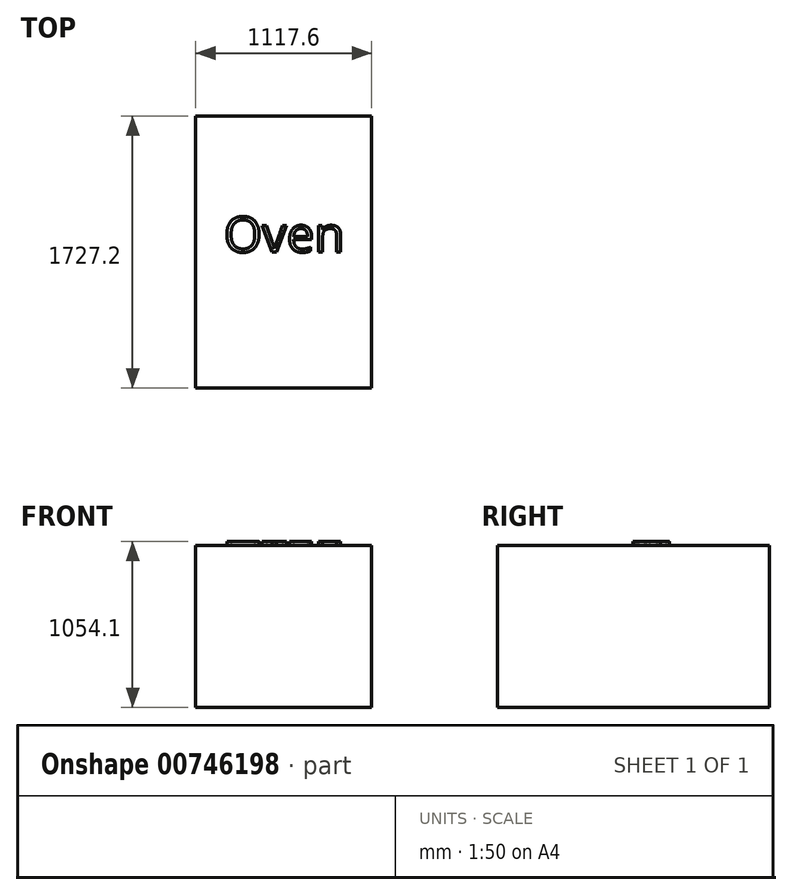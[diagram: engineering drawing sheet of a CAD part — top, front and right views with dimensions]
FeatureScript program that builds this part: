
annotation { "Feature Type Name" : "Feature", "Feature Type Description" : "" }
export const myFeature = defineFeature(function(context is Context, id is Id, definition is map)
    precondition{}
    {
        {
            var Q0;
            Q0=qCreatedBy(makeId("Top.planeOp"),FACE);
            var sketch = newSketch(context, id + "F0", { "sketchPlane" : qUnion([Q0])});
            skLineSegment(sketch, "E0.bottom", {"start": v(558.8, -863.6) * mm, "end": v(-558.8, -863.6) * mm});
            skLineSegment(sketch, "E0.top", {"start": v(558.8, 863.6) * mm, "end": v(-558.8, 863.6) * mm});
            skLineSegment(sketch, "E0.left", {"start": v(558.8, -863.6) * mm, "end": v(558.8, 863.6) * mm});
            skLineSegment(sketch, "E0.right", {"start": v(-558.8, -863.6) * mm, "end": v(-558.8, 863.6) * mm});
            skPoint(sketch, "E0.middle", {"position": v(0, 0) * mm});
            skSolve(sketch);
        }
        {
            var Q0;
            Q0 = qSketchRegion(id + "F0", true);
            extrude(context, id + "F1", {"entities" : qUnion([Q0]), "depth" : 1028.7 * mm, "offsetDistance" : 25.4 * mm});
        }
        {
            var Q0;
            Q0=makeQuery(id+"F1.opExtrude","CAP_FACE",FACE,{"disambiguationData":[OSD([sQuery(id+"F0.wireOp",EDGE,"E0.bottom"),sQuery(id+"F0.wireOp",EDGE,"E0.top"),sQuery(id+"F0.wireOp",EDGE,"E0.left"),sQuery(id+"F0.wireOp",EDGE,"E0.right")])],"isStart":false});
            var sketch = newSketch(context, id + "F2", { "sketchPlane" : qUnion([Q0])});
            skText(sketch, "E1", { "text": "Oven", "fontName": "OpenSans-Regular.ttf"});
            const initialGuessF2  = {"E1": [-0.381, 0, 1, 0, 0.22495]};
            skSetInitialGuess(sketch, initialGuessF2);
            skSolve(sketch);
        }
        {
            var Q0;
            Q0 = qSketchRegion(id + "F2", true);
            extrude(context, id + "F3", {"entities" : qUnion([Q0]), "operationType" : NewBodyOperationType.ADD, "depth" : 25.4 * mm, "offsetDistance" : 25.4 * mm});
        }
    });
